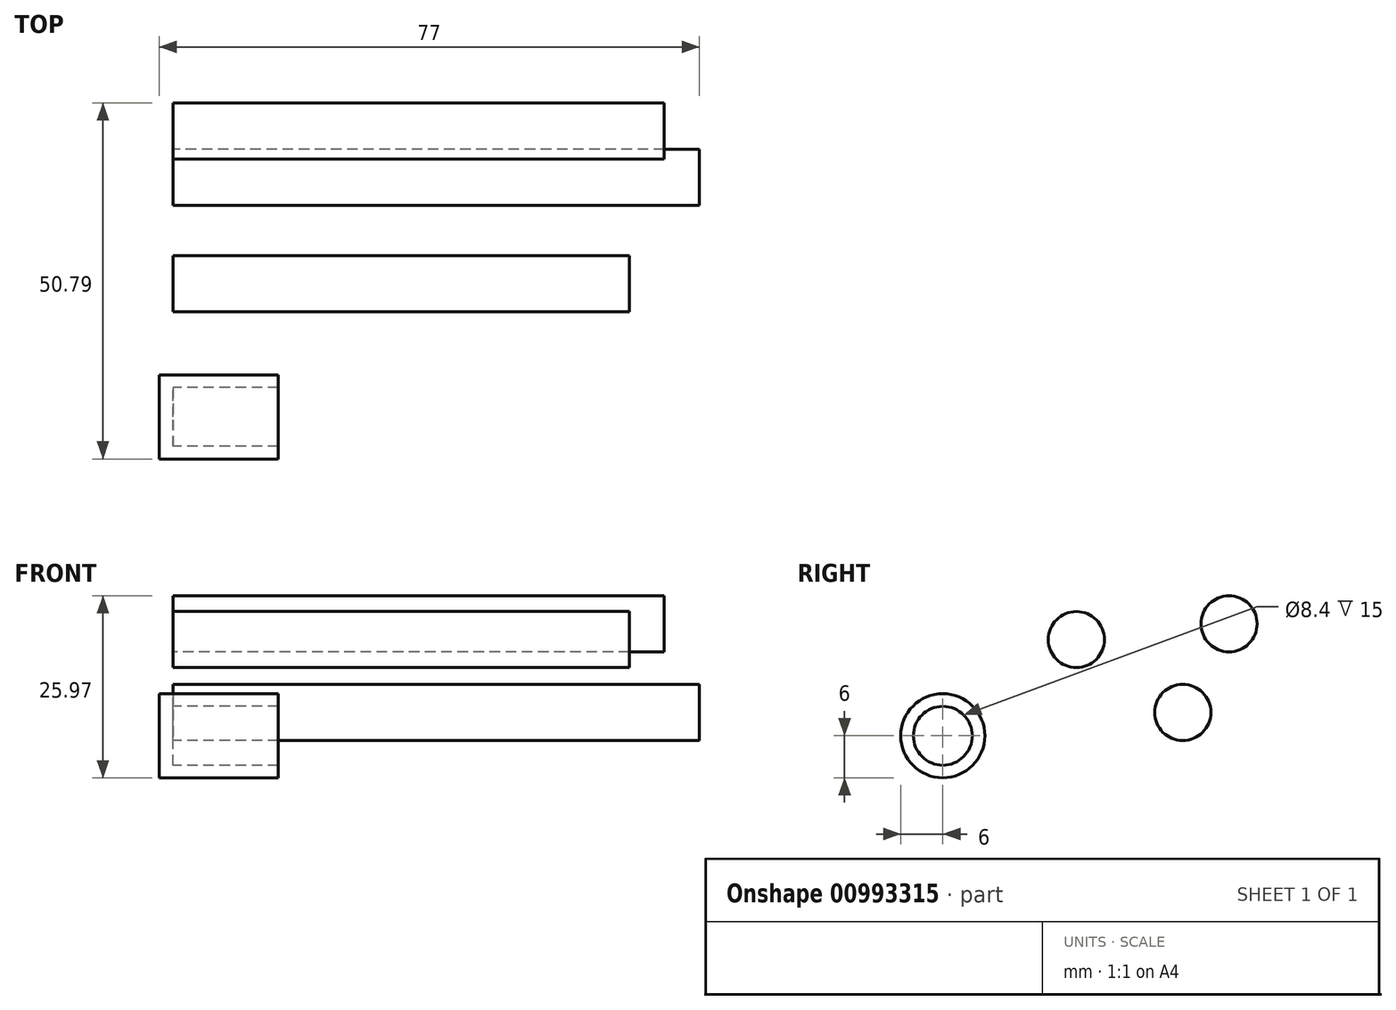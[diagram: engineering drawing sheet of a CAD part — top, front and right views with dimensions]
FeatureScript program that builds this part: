
annotation { "Feature Type Name" : "Feature", "Feature Type Description" : "" }
export const myFeature = defineFeature(function(context is Context, id is Id, definition is map)
    precondition{}
    {
        {
            var Q0;
            Q0=qCreatedBy(makeId("Right.planeOp"),FACE);
            var sketch = newSketch(context, id + "F0", { "sketchPlane" : qUnion([Q0])});
            skCircle(sketch, "E0", {"center": v(0, 0) * mm, "radius": 4.2 * mm});
            skCircle(sketch, "E1", {"center": v(0, 0) * mm, "radius": 6 * mm});
            skCircle(sketch, "E2", {"center": v(34.2, 3.32) * mm, "radius": 4 * mm});
            skCircle(sketch, "E3", {"center": v(19.03, 13.72) * mm, "radius": 4 * mm});
            skCircle(sketch, "E4", {"center": v(40.8, 15.97) * mm, "radius": 4 * mm});
            skSolve(sketch);
        }
        {
            var Q0;
            Q0=makeQuery(id+"F0.imprint","IMPRINT",FACE,{"disambiguationData":[TD([[makeQuery(id+"F0.imprint","IMPRINT",EDGE,{"derivedFrom":sQuery(id+"F0.wireOp",EDGE,"E0")}),-1.0]])]});
            extrude(context, id + "F1", {"entities" : qUnion([Q0]), "depth" : 15 * mm, "offsetDistance" : 25 * mm});
        }
        {
            var Q0;
            Q0=makeQuery(id+"F0.imprint","IMPRINT",FACE,{"disambiguationData":[TD([[makeQuery(id+"F0.imprint","IMPRINT",EDGE,{"derivedFrom":sQuery(id+"F0.wireOp",EDGE,"E0")}),1.0]])]});
            var Q1;
            Q1=makeQuery(id+"F0.imprint","IMPRINT",FACE,{"disambiguationData":[TD([[makeQuery(id+"F0.imprint","IMPRINT",EDGE,{"derivedFrom":sQuery(id+"F0.wireOp",EDGE,"E0")}),-1.0]])]});
            extrude(context, id + "F2", {"entities" : qUnion([Q0, Q1]), "operationType" : NewBodyOperationType.ADD, "oppositeDirection" : true, "depth" : 2 * mm, "offsetDistance" : 25 * mm});
        }
        {
            var Q0;
            Q0=makeQuery(id+"F0.imprint","IMPRINT",FACE,{"disambiguationData":[TD([[makeQuery(id+"F0.imprint","IMPRINT",EDGE,{"derivedFrom":sQuery(id+"F0.wireOp",EDGE,"E2")}),1.0]])]});
            extrude(context, id + "F3", {"entities" : qUnion([Q0]), "depth" : 75 * mm, "offsetDistance" : 25 * mm});
        }
        {
            var Q0;
            Q0=makeQuery(id+"F0.imprint","IMPRINT",FACE,{"disambiguationData":[TD([[makeQuery(id+"F0.imprint","IMPRINT",EDGE,{"derivedFrom":sQuery(id+"F0.wireOp",EDGE,"E3")}),1.0]])]});
            extrude(context, id + "F4", {"entities" : qUnion([Q0]), "depth" : 65 * mm, "offsetDistance" : 25 * mm});
        }
        {
            var Q0;
            Q0=makeQuery(id+"F0.imprint","IMPRINT",FACE,{"disambiguationData":[TD([[makeQuery(id+"F0.imprint","IMPRINT",EDGE,{"derivedFrom":sQuery(id+"F0.wireOp",EDGE,"E4")}),1.0]])]});
            extrude(context, id + "F5", {"entities" : qUnion([Q0]), "depth" : 70 * mm, "offsetDistance" : 25 * mm});
        }
    });
